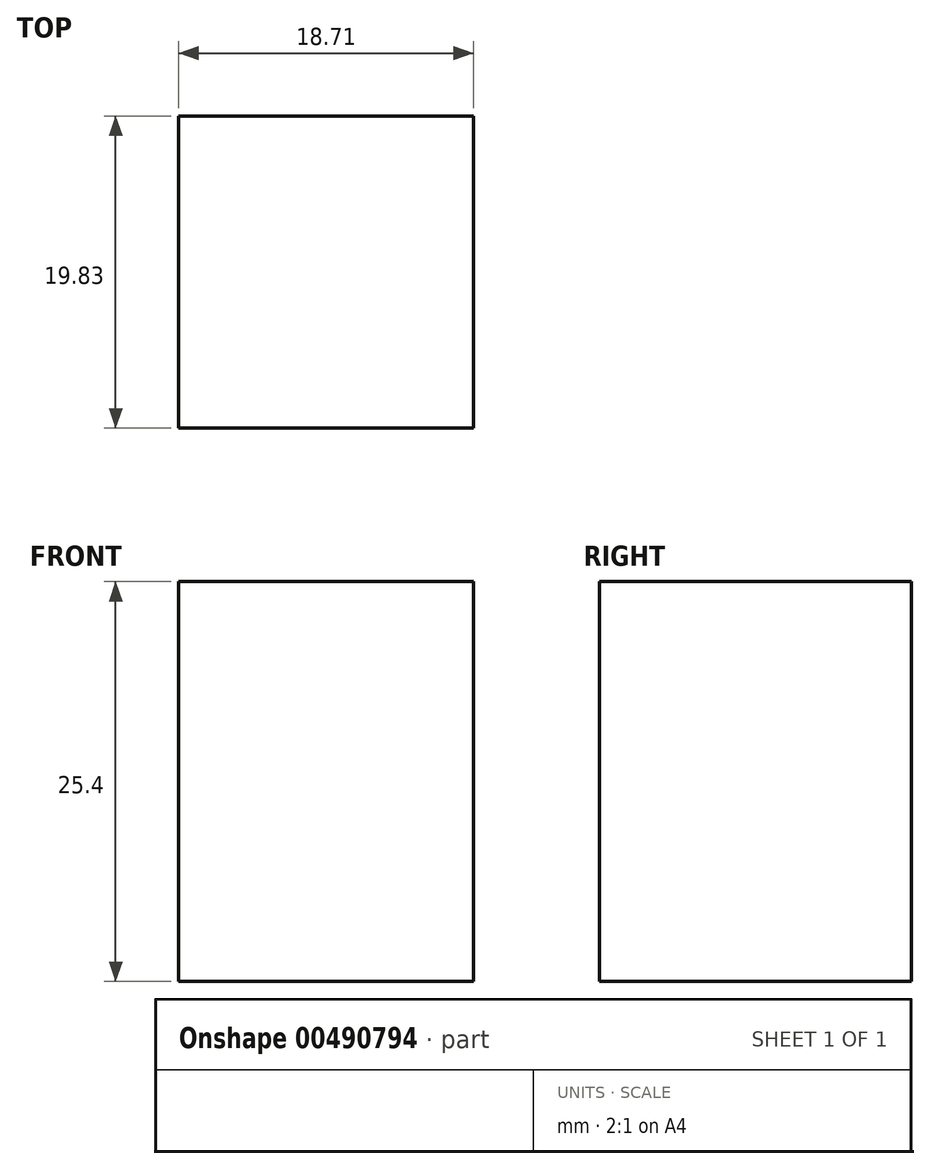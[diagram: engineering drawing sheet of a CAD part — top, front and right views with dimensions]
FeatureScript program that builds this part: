
annotation { "Feature Type Name" : "Feature", "Feature Type Description" : "" }
export const myFeature = defineFeature(function(context is Context, id is Id, definition is map)
    precondition{}
    {
        {
            var Q0;
            Q0=qCreatedBy(makeId("Top.planeOp"),FACE);
            var sketch = newSketch(context, id + "F0", { "sketchPlane" : qUnion([Q0])});
            skLineSegment(sketch, "E0.bottom", {"start": v(15.78, 19.4) * mm, "end": v(34.49, 19.4) * mm});
            skLineSegment(sketch, "E0.top", {"start": v(15.78, 39.24) * mm, "end": v(34.49, 39.24) * mm});
            skLineSegment(sketch, "E0.left", {"start": v(15.78, 19.4) * mm, "end": v(15.78, 39.24) * mm});
            skLineSegment(sketch, "E0.right", {"start": v(34.49, 19.4) * mm, "end": v(34.49, 39.24) * mm});
            skSolve(sketch);
        }
        {
            var Q0;
            Q0=makeQuery(id+"F0.imprint","IMPRINT",FACE,{"disambiguationData":[TD([[makeQuery(id+"F0.imprint","IMPRINT",EDGE,{"derivedFrom":sQuery(id+"F0.wireOp",EDGE,"E0.bottom")}),1.0]])]});
            extrude(context, id + "F1", {"entities" : qUnion([Q0]), "depth" : 25.4 * mm});
        }
    });
